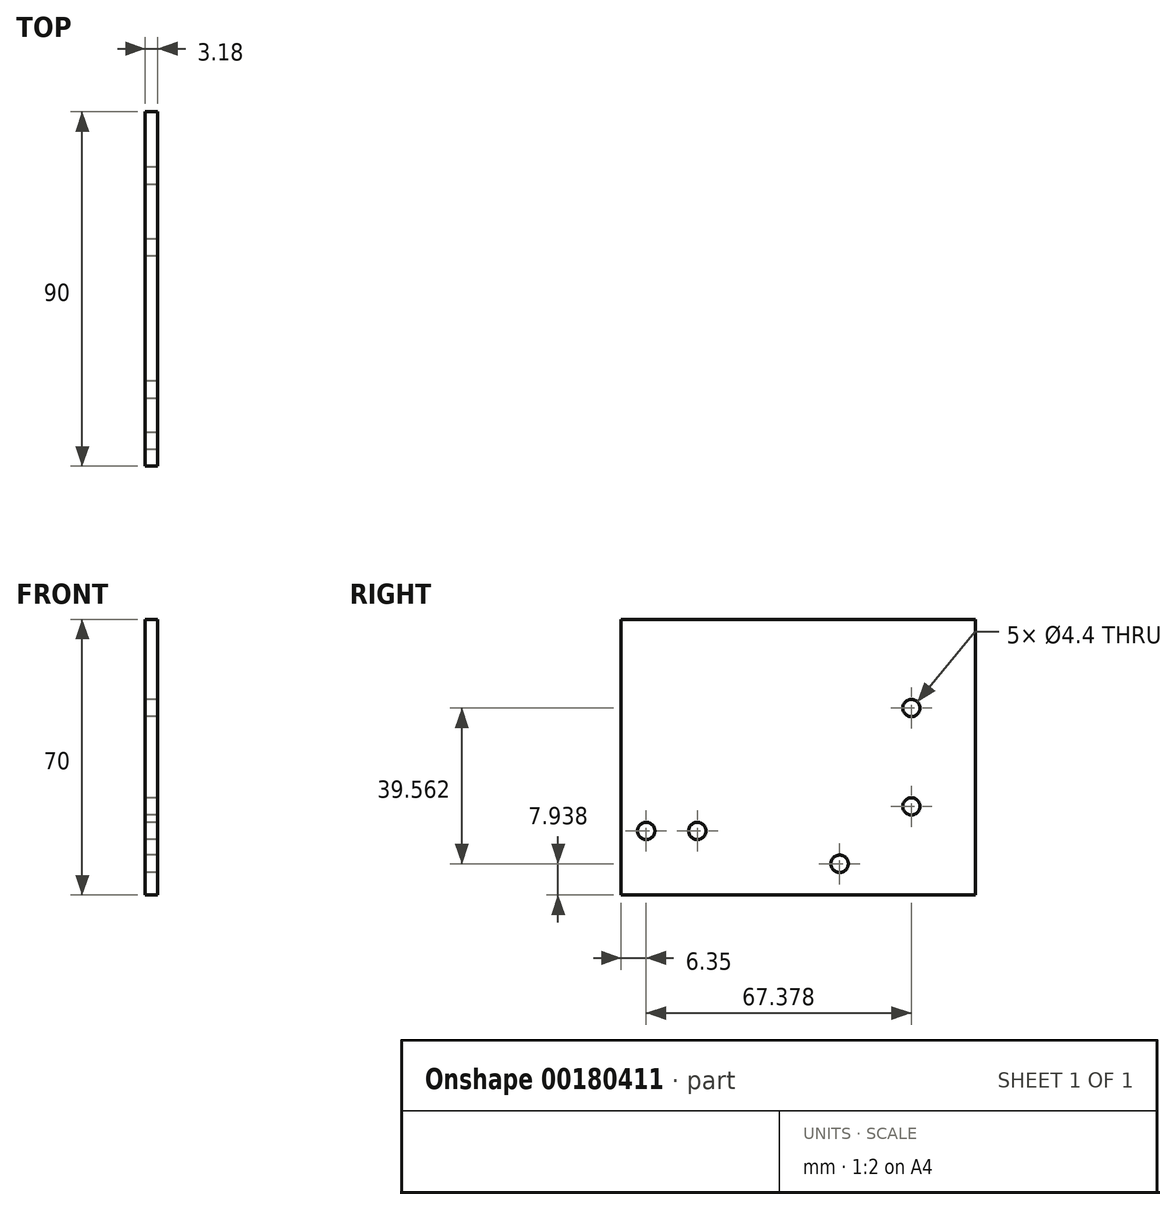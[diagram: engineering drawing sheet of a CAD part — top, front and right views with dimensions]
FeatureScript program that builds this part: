
annotation { "Feature Type Name" : "Feature", "Feature Type Description" : "" }
export const myFeature = defineFeature(function(context is Context, id is Id, definition is map)
    precondition{}
    {
        {
            var Q0;
            Q0=qCreatedBy(makeId("Top.planeOp"),FACE);
            var sketch = newSketch(context, id + "F0", { "sketchPlane" : qUnion([Q0])});
            skLineSegment(sketch, "E0.bottom", {"start": v(1.59, -45) * mm, "end": v(-1.59, -45) * mm});
            skLineSegment(sketch, "E0.top", {"start": v(1.59, 45) * mm, "end": v(-1.59, 45) * mm});
            skLineSegment(sketch, "E0.left", {"start": v(1.59, -45) * mm, "end": v(1.59, 45) * mm});
            skLineSegment(sketch, "E0.right", {"start": v(-1.59, -45) * mm, "end": v(-1.59, 45) * mm});
            skPoint(sketch, "E0.middle", {"position": v(0, 0) * mm});
            skSolve(sketch);
        }
        {
            var Q0;
            Q0 = qSketchRegion(id + "F0", true);
            extrude(context, id + "F1", {"entities" : qUnion([Q0]), "depth" : 70 * mm});
        }
        {
            var Q0;
            Q0=makeQuery(id+"F1.opExtrude","SWEPT_FACE",FACE,{"disambiguationData":[OSD([sQuery(id+"F0.wireOp",EDGE,"E0.right")])]});
            var sketch = newSketch(context, id + "F2", { "sketchPlane" : qUnion([Q0])});
            skPoint(sketch, "E1", {"position": v(-28.73, 47.5) * mm});
            skPoint(sketch, "E2", {"position": v(-28.73, 22.5) * mm});
            skSolve(sketch);
        }
        {
            var Q0;
            Q0=sQuery(id+"F2.wireOp",VERTEX,"E1");
            var Q1;
            Q1=sQuery(id+"F2.wireOp",VERTEX,"E2");
            var Q2;
            Q2=makeQuery(id+"F1.opExtrude","SWEPT_BODY",BODY,{"disambiguationData":[OSD([sQuery(id+"F0.wireOp",EDGE,"E0.bottom"),sQuery(id+"F0.wireOp",EDGE,"E0.top"),sQuery(id+"F0.wireOp",EDGE,"E0.left"),sQuery(id+"F0.wireOp",EDGE,"E0.right")])]});
            hole(context, id + "F3", {"style" : HoleStyle.SIMPLE, "endStyle" : HoleEndStyle.THROUGH, "standardTappedOrClearance" : lookupTablePath({ "standard" : "ISO", "fit" : "Normal", "size" : "M4", "type" : "Clearance" }), "standardBlindInLast" : lookupTablePath({ "fit" : "Standard", "standard" : "ISO", "size" : "M4", "type" : "Clearance" }), "holeDiameter" : 4.4 * mm, "locations" : qUnion([Q0, Q1]), "scope" : qUnion([Q2]), "isTappedThrough" : true});
        }
        {
            var Q0;
            Q0=makeQuery(id+"F1.opExtrude","SWEPT_FACE",FACE,{"disambiguationData":[OSD([sQuery(id+"F0.wireOp",EDGE,"E0.right")])]});
            var sketch = newSketch(context, id + "F4", { "sketchPlane" : qUnion([Q0])});
            skPoint(sketch, "E3", {"position": v(38.65, 16.27) * mm});
            skPoint(sketch, "E4", {"position": v(25.65, 16.27) * mm});
            skPoint(sketch, "E5", {"position": v(-10.5, 7.94) * mm});
            skSolve(sketch);
        }
        {
            var Q0;
            Q0=sQuery(id+"F4.wireOp",VERTEX,"E3");
            var Q1;
            Q1=sQuery(id+"F4.wireOp",VERTEX,"E4");
            var Q2;
            Q2=sQuery(id+"F4.wireOp",VERTEX,"E5");
            var Q3;
            Q3=makeQuery(id+"F1.opExtrude","SWEPT_BODY",BODY,{"disambiguationData":[OSD([sQuery(id+"F0.wireOp",EDGE,"E0.bottom"),sQuery(id+"F0.wireOp",EDGE,"E0.top"),sQuery(id+"F0.wireOp",EDGE,"E0.left"),sQuery(id+"F0.wireOp",EDGE,"E0.right")])]});
            hole(context, id + "F5", {"style" : HoleStyle.SIMPLE, "endStyle" : HoleEndStyle.BLIND, "standardTappedOrClearance" : lookupTablePath({ "standard" : "ISO", "fit" : "Normal", "size" : "M4", "type" : "Clearance" }), "standardBlindInLast" : lookupTablePath({ "fit" : "Standard", "standard" : "ISO", "size" : "M4", "type" : "Clearance" }), "holeDiameter" : 4.4 * mm, "holeDepth" : 25 * mm, "locations" : qUnion([Q0, Q1, Q2]), "scope" : qUnion([Q3])});
        }
    });
